# Revit family: ONNSA
name_source: partatom
category: Mechanical Equipment
units: mm (PartAtom-declared; Revit-internal decimal feet)

## family parameters
Always vertical = Yes
Cut with Voids When Loaded = No
OmniClass Number = 23.40.40.11.17
OmniClass Title = Refrigerated Cases
Part Type = Normal
Room Calculation Point = No
Round Connector Dimension = Use Radius
Shared = No
Work Plane-Based = Yes

## types (5) — shared parameters
12" Shelf = Yes
BOTTOM ELECTRICAL = Yes
BOTTOM REFRIGERATION PIPING = Yes
Certifications = NSF 7, UL471, CSA
DATE = 05/17/2016
DESIGNERS NAME = SHIDDRAMESH
DRAIN PIPING = Yes
Default Elevation = 48"
Description = Narrow Multi-Deck Self-Contained Merchandiser
EQUIPMENT DESCRIPTION = Narrow Multi-Deck Self-Contained Merchandiser
EQUIPMENT MARK = ONNSA
GLASS = Glass
Height = 85 1/2"
High Power (Cornice) Amps = 0 A
Item Description = Narrow Multi-Deck Self-Contained Merchandiser
Keynote = ONNSA
LF STD END = Yes
Legend Number = ONNSA
Manufacturer = HILL PHOENIX
Model = ONNSA
PAINTED METAL UPPER SHELF = PAINTED SHELVES
REAR REFRIGERATION PIPING = Yes
REFRIGERATION PIPING = COPPER PIPE
RT STD END = Yes
Refrigerant = R134A
STAINLESS STEEL = GALVANIZED STEEL
Standard Power Amps = 0 A
System Amperage = 30 A
Systems Frequency = 60 Hz
TOP ELECTRICAL = Yes
TOP REFRIGERATION PIPING = Yes
URL = http://www.hillphoenix.com
Width = 22 7/8"

## per-type parameters (varying)
| type | 24 hour Energy Usage (kWh) | CENTER LINE & DRAIN | Defrosts Per Day | Discharge Air (°F) | Discharge Air Velocity (FPM) | High Power (Cornice) Watts | Length | Light Length | Lights Per Row | Locked Rotor (LRA) Amps | Plug Style | Running Load (RLA) Amps | Standard Power Watts | Suction Pressure @ Case Outlet (psig) | Superheat Set Point @ Bulb (°F) | System Data Phase | System Data Volts | Systems Horsepower | Timed-Off Defrost Fail-Safe (Min) | Timed-Off Defrost Termination Temp |
| 4' case | 37.2 | 23 1/2" | 6 | 35 °F | 275 FPM | 15 W | 47" | 3' | 1 | 67 A | NEMA L5-30 | 13 A | 8 W | 19.90 psi | 6-8 | 1 | 120 V | 1/2 | 28 | 52 °F |
| 6' case | 50 | 34 5/8" | 6 | 31 °F | 230 FPM | 12 W | 69 1/4" | 3' | 2 | 77 A | NEMA L5-30 | 15 A | 5 W | 59.00 psi | 6-8  °F | 1 | 208 V | 1 | 28 | 52 °F |
| 8' case | 63.0 | 46 5/8" | 6 | 31 °F | 230 FPM | 11 W | 93 1/4" | 2' | 2 | 51 A | NEMA L14-30 | 11 A | 6 W | 59.00 psi | 6-8  °F | 3 | 208 V | 1-1/2 | 40 (Min) | 47 °F |
| 3' case | 37.2 | 18" | 6 | 35 °F | 275 FPM | 15 W | 36" | 3' | 1 | 67 A | NEMA L5-30 | 13 A | 8 W | 19.90 psi | 6-8 | 1 | 120 V | 1/2 | 28 | 52 °F |
| 6' case 2 | 50 | 34 5/8" | 24 | 31 °F | 230 FPM | 12 W | 69 1/4" | 3' | 2 | 43 A | NEMA L5-30 | 9 A | 5 W | 59.00 psi | 6-8  °F | 3 | 208 V | 1 | 9 (Min) | 37 °F |

## geometry (parser evidence)
native form markers: Blend x10, Sweep x2
no freeform markers — native parametric forms only
